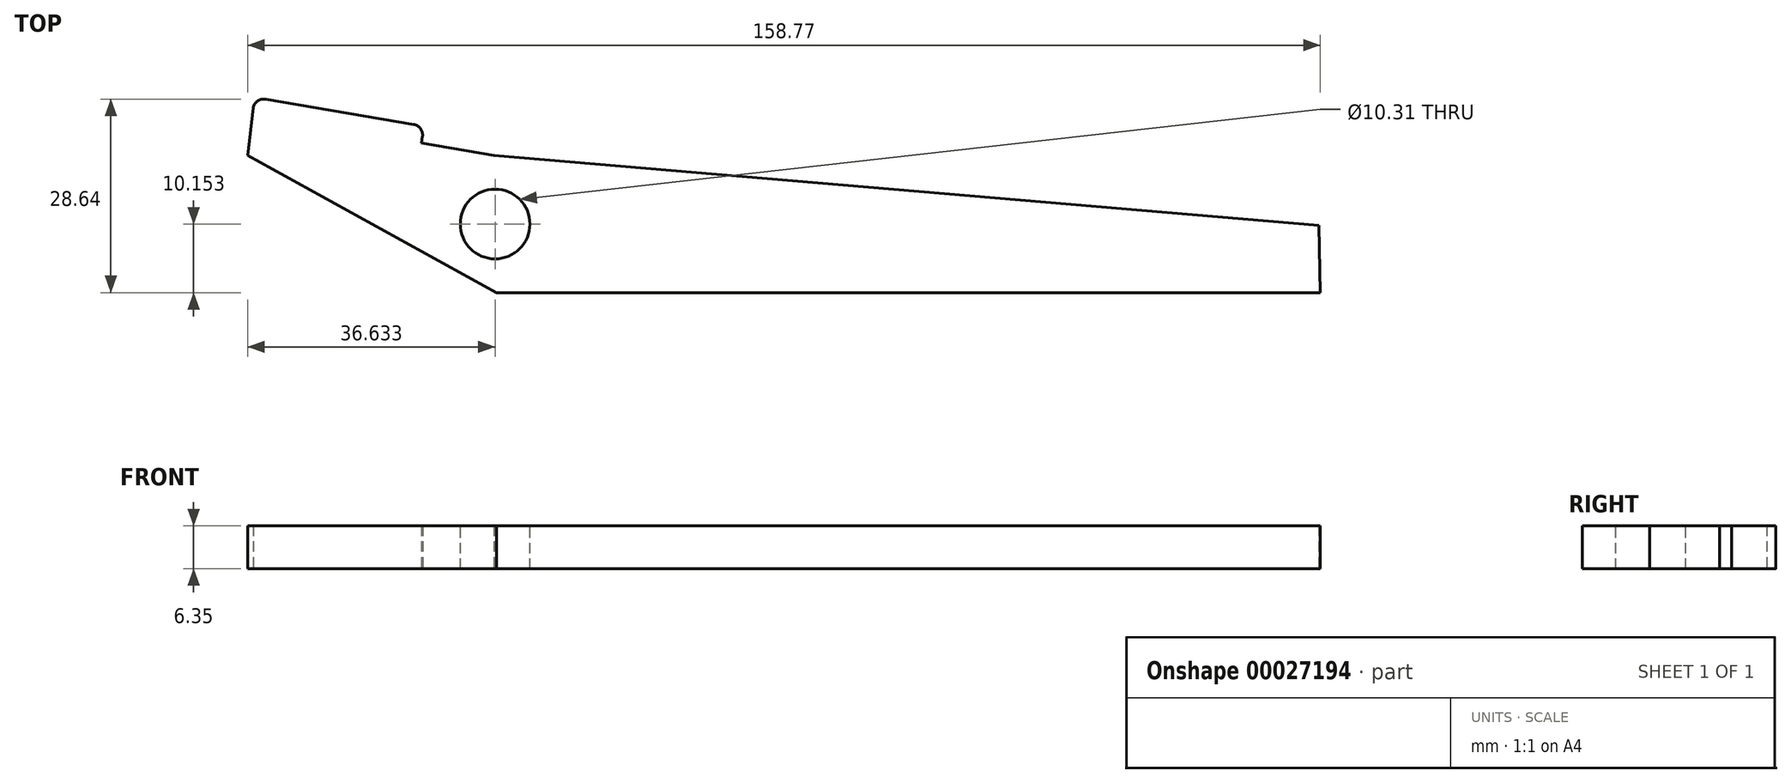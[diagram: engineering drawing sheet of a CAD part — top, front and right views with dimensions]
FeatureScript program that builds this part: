
annotation { "Feature Type Name" : "Feature", "Feature Type Description" : "" }
export const myFeature = defineFeature(function(context is Context, id is Id, definition is map)
    precondition{}
    {
        {
            var Q0;
            Q0=qCreatedBy(makeId("Top.planeOp"),FACE);
            var sketch = newSketch(context, id + "F0", { "sketchPlane" : qUnion([Q0])});
            skLineSegment(sketch, "E0.top", {"start": v(-17.35, 16.43) * mm, "end": v(104.6, 16.43) * mm});
            skLineSegment(sketch, "E0.right", {"start": v(104.4, 26.41) * mm, "end": v(104.6, 16.43) * mm});
            skLineSegment(sketch, "E1.0", {"start": v(-17.74, 36.74) * mm, "end": v(-17.35, 16.43) * mm});
            skLineSegment(sketch, "E2", {"start": v(-17.74, 36.74) * mm, "end": v(104.4, 26.41) * mm});
            skLineSegment(sketch, "E3", {"start": v(-28.47, 38.56) * mm, "end": v(-17.74, 36.74) * mm});
            skLineSegment(sketch, "E4", {"start": v(-17.35, 16.43) * mm, "end": v(-54.18, 36.75) * mm});
            skLineSegment(sketch, "E5.0", {"start": v(-51.53, 45.05) * mm, "end": v(-29.6, 41.33) * mm});
            skLineSegment(sketch, "E6", {"start": v(-28.3, 39.51) * mm, "end": v(-28.47, 38.56) * mm});
            skPoint(sketch, "E7.visualSharp", {"position": v(-27.3, 47.77) * mm});
            skArc(sketch, "E7.filletArc", {"start": v(-28.3, 39.51) * mm, "mid": v(-28.57, 40.69) * mm, "end": v(-29.6, 41.33) * mm});
            skPoint(sketch, "E8.visualSharp", {"position": v(-52.7, 48.1) * mm});
            skArc(sketch, "E8.filletArc", {"start": v(-51.53, 45.05) * mm, "mid": v(-52.7, 44.78) * mm, "end": v(-53.35, 43.76) * mm});
            skPoint(sketch, "E0.left.start.orphan", {"position": v(-52.74, 45.68) * mm});
            skLineSegment(sketch, "E9", {"start": v(-53.35, 43.76) * mm, "end": v(-54.18, 36.75) * mm});
            skLineSegment(sketch, "E10", {"start": v(104.6, 16.43) * mm, "end": v(-67.28, 16.43) * mm});
            skSolve(sketch);
        }
        {
            var Q0;
            Q0=makeQuery(id+"F0.imprint","IMPRINT",FACE,{"disambiguationData":[TD([[makeQuery(id+"F0.imprint","IMPRINT",EDGE,{"derivedFrom":sQuery(id+"F0.wireOp",EDGE,"E1.0")}),-1.0]])]});
            var Q1;
            Q1=makeQuery(id+"F0.imprint","IMPRINT",FACE,{"disambiguationData":[TD([[makeQuery(id+"F0.imprint","IMPRINT",EDGE,{"derivedFrom":sQuery(id+"F0.wireOp",EDGE,"E0.top")}),1.0]])]});
            var Q2;
            {var subQ0=sQuery(id+"F0.wireOp",EDGE,"E0.right");Q2=makeQuery(id+"F0.imprint","IMPRINT",FACE,{"disambiguationData":[TD([[makeQuery(id+"F0.imprint","IMPRINT",EDGE,{"derivedFrom":subQ0}),-1.0]])]});}
            extrude(context, id + "F1", {"entities" : qUnion([Q0, Q1, Q2]), "depth" : 6.35 * mm, "offsetDistance" : 25.4 * mm});
        }
        {
            var Q0;
            Q0=makeQuery(id+"F1.opExtrude","CAP_FACE",FACE,{"disambiguationData":[OSD([sQuery(id+"F0.wireOp",EDGE,"E0.top"),sQuery(id+"F0.wireOp",EDGE,"E0.left"),sQuery(id+"F0.wireOp",EDGE,"E0.right"),sQuery(id+"F0.wireOp",EDGE,"E2"),sQuery(id+"F0.wireOp",EDGE,"E3"),sQuery(id+"F0.wireOp",EDGE,"E4")])],"isStart":false});
            var sketch = newSketch(context, id + "F2", { "sketchPlane" : qUnion([Q0])});
            skLineSegment(sketch, "E11", {"start": v(-17.35, 16.43) * mm, "end": v(-17.74, 36.74) * mm});
            skPoint(sketch, "E12", {"position": v(-17.55, 26.58) * mm});
            skSolve(sketch);
        }
        {
            var Q0;
            Q0=sQuery(id+"F2.wireOp",VERTEX,"E12");
            var Q1;
            Q1=makeQuery(id+"F1.opExtrude","SWEPT_BODY",BODY,{"disambiguationData":[OSD([sQuery(id+"F0.wireOp",EDGE,"E0.top"),sQuery(id+"F0.wireOp",EDGE,"E0.left"),sQuery(id+"F0.wireOp",EDGE,"E0.right"),sQuery(id+"F0.wireOp",EDGE,"E2"),sQuery(id+"F0.wireOp",EDGE,"E3"),sQuery(id+"F0.wireOp",EDGE,"E4")])]});
            hole(context, id + "F3", {"style" : HoleStyle.SIMPLE, "endStyle" : HoleEndStyle.THROUGH, "holeDiameter" : 10.3 * mm, "majorDiameter" : 6.35 * mm, "isTappedThrough" : true, "tappedDepth" : 19.05 * mm, "tapClearance" : 3, "startFromSketch" : true, "locations" : qUnion([Q0]), "scope" : qUnion([Q1])});
        }
    });
